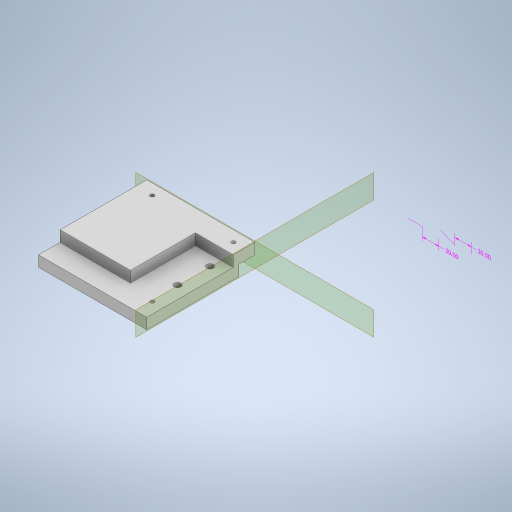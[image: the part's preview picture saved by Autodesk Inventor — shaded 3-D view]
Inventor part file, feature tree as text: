
AUTODESK INVENTOR PART (.ipt)
format: ipt  version: 2023 (Build 270158000, 158)  size: 374,272 bytes
history: native  units: mm
features: sketch x8, extrude x5, other x4, hole x3, plane x2, split x2
ambient origin geometry x8: Origin, YZ Plane, XZ Plane, XY Plane, X Axis, Y Axis, Z Axis, Center Point
bodies: Body1 (feature_tree)
feature tree (24):
  other  "Sólido1"
  other  "Anotaciones"
  extrude  "Extrusión1"  Depth=200.0mm
  extrude  "Extrusión2"  Depth=10.0mm TaperAngle=0.0deg
  extrude  "Extrusión3"  Depth=20.0mm
  hole  "Agujero1"  [1 undecoded]
  extrude  "Extrusión4"  Depth=10.0mm
  plane  "Plano de trabajo1"
  plane  "Plano de trabajo2"
  hole  "Agujero2"  [1 undecoded]
  extrude  "Extrusión5"  Depth=10.0mm TaperAngle=0.0deg
  hole  "Agujero3"  [1 undecoded]
  split  "Dividir3"
  split  "Dividir4"
  sketch  "Boceto1"  dims[d0=200.0mm d1=200.0mm]
  sketch  "Boceto2"  dims[d2=20.0mm d3=0.0mm]
  sketch  "Boceto3"  dims[d4=20.0mm d5=20.0mm d6=30.0mm d7=30.0mm d8=20.0mm d9=35.0mm d10=35.0mm d11=60.0mm d12=10.0mm d13=0.0mm]
  sketch  "Boceto4"  dims[d14=20.0mm d15=0.0mm]
  sketch  "Boceto5"  dims[d16=3.5mm d18=1.75mm d19=1.75mm d20=1.75mm d21=1.75mm d22=10.0mm d23=10.0mm d25=20.0mm]
  sketch  "Boceto7"  dims[d26=40.0mm d27=40.0mm]
  sketch  "Boceto8"  dims[d28=3.5mm d29=6.0mm d30=4.0mm d31=2.0mm d32=90.0deg d33=8.0mm d34=20.594885mm d38=10.0mm]
  sketch  "Boceto9"  dims[d39=10.0mm d40=40.0mm d41=10.0mm d42=0.0mm d52=3.5mm d54=10.0mm d55=10.0mm d56=3.5mm d57=6.0mm d58=4.0mm d59=2.0mm d60=90.0deg d61=8.0mm d62=20.594885mm d63=30.0mm d64=30.0mm d65=10.0mm d66=0.0mm d67=3.5mm d68=15.0mm d69=10.0mm d70=45.0deg d71=45.0deg d72=3.5mm d73=6.0mm d74=4.0mm d75=2.0mm d76=90.0deg d77=8.0mm d78=20.594885mm d43=6.672192mm d44=4.931866mm d45=30.0mm d46=5.890777mm d47=4.508932mm d48=30.0mm d83=0.5mm d84=0.872665mm d85=0.5mm d86=0.872665mm]
  other  "Cota lineal 1"
  other  "Cota lineal 2"
note: 3 required parameter values undecoded (feature->parameter linkage not recoverable at this tier; creation-order binding heuristic only, values carry confidence <= 0.55)
